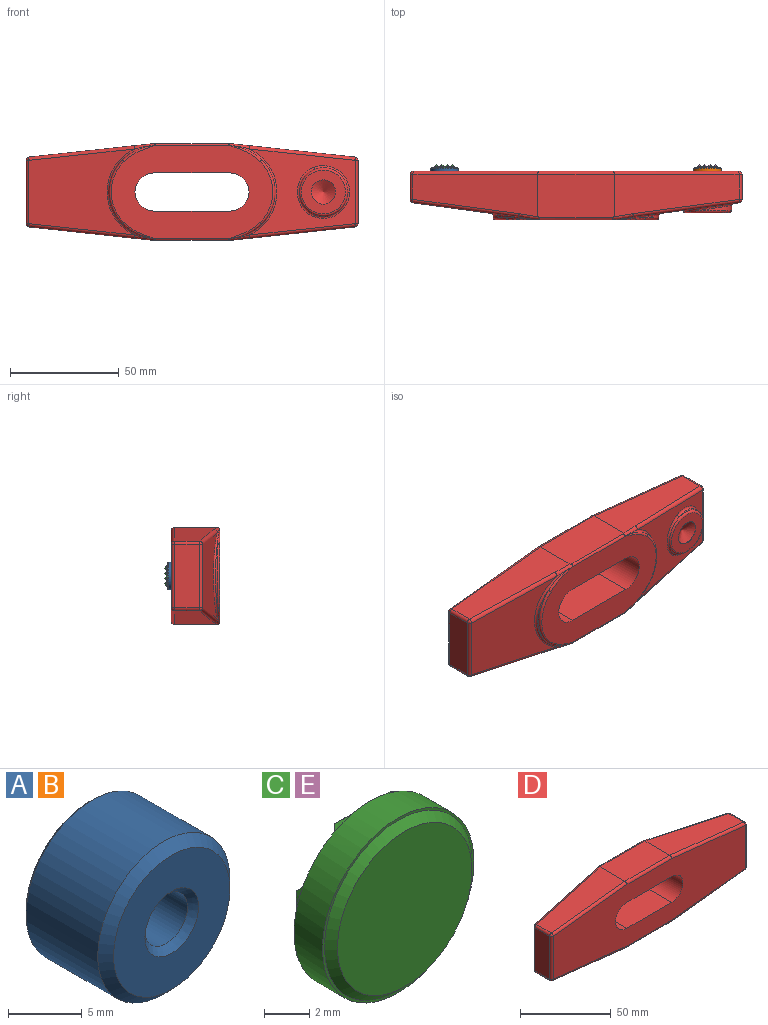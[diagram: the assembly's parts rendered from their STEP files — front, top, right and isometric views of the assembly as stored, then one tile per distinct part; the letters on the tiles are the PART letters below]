
ASSEMBLY  parts=5 mates=4
PART A: 14 faces, bbox 12.7x7.9x12.7 mm
  f0: cone r=2.04mm half-angle=45deg, axis (0,1,0), area 8.7mm2, adj f1,f10
  f1: cylinder r=2.04mm len=5.39mm, axis (0,1,0), area 69.2mm2, adj f0,f2
  f2: cone r=2.58mm half-angle=45deg, axis (0,-1,0), area 11mm2, adj f1,f8
  f3: cylinder r=4.9mm len=9.8mm, axis (0,1,0), area 39.9mm2, adj f4,f10
  f4: cone r=5.16mm half-angle=45deg, axis (0,1,0), area 11.4mm2, adj f3,f9
  f5: cone r=6.35mm half-angle=45deg, axis (0,-1,0), area 14mm2, adj f6,f9
  f6: cylinder r=6.35mm len=12.7mm, axis (0,1,0), area 245.8mm2, adj f5,f7,f11,f12,f13
  f7: cone r=5.59mm half-angle=45deg, axis (0,1,0), area 40.4mm2, adj f6,f8
  f8: plane 11.18x11.18mm, normal (0,-1,0), area 77.2mm2, adj f2,f7
  f9: plane 12.19x12.19mm, normal (0,1,0), area 33.2mm2, adj f4,f5
  f10: plane 9.8x9.8mm, normal (0,1,0), area 56.2mm2, adj f0,f3
  f11: plane 6.89x1.02mm, normal (0,1,0), area 4.7mm2, adj f6,f12
  f12: plane 6.89x3.96mm, normal (1,0,0), area 27.3mm2, adj f6,f11,f13
  f13: plane 6.89x1.02mm, normal (0,-1,0), area 4.7mm2, adj f6,f12
PART B: same geometry as A
PART C: 61 faces, bbox 9.5x3.2x9.5 mm
  f0: cone r=4.2mm half-angle=45deg, axis (0,1,0), area 15.9mm2, adj f38,f39
  f1: cylinder r=4.74mm len=9.47mm, axis (0,-1,0), area 52.9mm2, adj f39,f40
  f2: plane 1.46x0.9mm, normal (0,0.71,0.71), area 0.8mm2, adj f24,f25,f53
  f3: plane 1.46x0.9mm, normal (0,0.71,0.71), area 0.8mm2, adj f22,f23,f54
  f4: plane 1.46x0.9mm, normal (0,0.71,-0.71), area 0.8mm2, adj f18,f21,f55
  f5: plane 1.46x0.9mm, normal (0,0.71,-0.71), area 0.8mm2, adj f19,f20,f56
  f6: plane 1.55x1mm, normal (0,0.71,-0.71), area 1.2mm2, adj f17,f40,f49,f57
  f7: plane 1.55x1mm, normal (0,0.71,-0.71), area 1.2mm2, adj f16,f40,f47,f58
  f8: plane 1.9x0.99mm, normal (0,0.71,0.71), area 1.4mm2, adj f17,f40,f49,f57
  f9: plane 1.9x0.99mm, normal (0,0.71,0.71), area 1.4mm2, adj f16,f40,f47,f58
  f10: plane 1.9x0.99mm, normal (0,0.71,-0.71), area 1.4mm2, adj f15,f40,f43,f59
  f11: plane 1.9x0.99mm, normal (0,0.71,-0.71), area 1.4mm2, adj f14,f40,f41,f60
  f12: plane 1.55x1mm, normal (0,0.71,0.71), area 1.2mm2, adj f15,f40,f43,f59
  f13: plane 1.55x1mm, normal (0,0.71,0.71), area 1.2mm2, adj f14,f40,f41,f60
  f14: plane 1.46x0.9mm, normal (-0.71,0.71,0), area 0.8mm2, adj f11,f13,f60
  f15: plane 1.46x0.9mm, normal (0.71,0.71,0), area 0.8mm2, adj f10,f12,f59
  f16: plane 1.46x0.9mm, normal (-0.71,0.71,0), area 0.8mm2, adj f7,f9,f58
  f17: plane 1.46x0.9mm, normal (0.71,0.71,0), area 0.8mm2, adj f6,f8,f57
  f18: plane 1.55x1mm, normal (-0.71,0.71,0), area 1.2mm2, adj f4,f28,f40,f55
  f19: plane 1.55x1mm, normal (0.71,0.71,0), area 1.2mm2, adj f5,f29,f40,f56
  f20: plane 1.9x0.99mm, normal (-0.71,0.71,0), area 1.4mm2, adj f5,f29,f40,f56
  f21: plane 1.9x0.99mm, normal (0.71,0.71,0), area 1.4mm2, adj f4,f28,f40,f55
  f22: plane 1.55x1mm, normal (0.71,0.71,0), area 1.2mm2, adj f3,f27,f40,f54
  f23: plane 1.9x0.99mm, normal (-0.71,0.71,0), area 1.4mm2, adj f3,f27,f40,f54
  f24: plane 1.9x0.99mm, normal (0.71,0.71,0), area 1.4mm2, adj f2,f26,f40,f53
  f25: plane 1.55x1mm, normal (-0.71,0.71,0), area 1.2mm2, adj f2,f26,f40,f53
  f26: plane 1.98x0.99mm, normal (0,0.71,-0.71), area 1.4mm2, adj f24,f25,f40
  f27: plane 1.98x0.99mm, normal (0,0.71,-0.71), area 1.4mm2, adj f22,f23,f40
  f28: plane 1.98x0.99mm, normal (0,0.71,0.71), area 1.4mm2, adj f18,f21,f40
  f29: plane 1.98x0.99mm, normal (0,0.71,0.71), area 1.4mm2, adj f19,f20,f40
  f30: plane 1.98x0.99mm, normal (0,0.71,-0.71), area 1.4mm2, adj f40,f48,f52
  f31: plane 1.98x0.99mm, normal (0,0.71,-0.71), area 1.4mm2, adj f40,f50,f51
  f32: plane 1.98x0.99mm, normal (0,0.71,0.71), area 1.4mm2, adj f40,f48,f52
  f33: plane 1.98x0.99mm, normal (0,0.71,0.71), area 1.4mm2, adj f40,f50,f51
  f34: plane 1.98x0.99mm, normal (0,0.71,-0.71), area 1.4mm2, adj f40,f42,f46
  f35: plane 1.98x0.99mm, normal (0,0.71,-0.71), area 1.4mm2, adj f40,f44,f45
  f36: plane 1.98x0.99mm, normal (0,0.71,0.71), area 1.4mm2, adj f40,f42,f46
  f37: plane 1.98x0.99mm, normal (0,0.71,0.71), area 1.4mm2, adj f40,f44,f45
  f38: plane 8.41x8.41mm, normal (0,-1,0), area 55.5mm2, adj f0
  f39: plane 9.47x9.47mm, normal (0,-1,0), area 3.7mm2, adj f0,f1
  f40: plane 9.47x9.47mm, normal (0,1,0), area 27.8mm2, adj f1,f6,f7,f8,f9,f10,f11,f12
  f41: plane 1.98x0.99mm, normal (0.71,0.71,0), area 1.4mm2, adj f11,f13,f40
  f42: plane 1.98x0.99mm, normal (-0.71,0.71,0), area 1.4mm2, adj f34,f36,f40
  f43: plane 1.98x0.99mm, normal (-0.71,0.71,0), area 1.4mm2, adj f10,f12,f40
  f44: plane 1.98x0.99mm, normal (0.71,0.71,0), area 1.4mm2, adj f35,f37,f40
  f45: plane 1.98x0.99mm, normal (-0.71,0.71,0), area 1.4mm2, adj f35,f37,f40
  f46: plane 1.98x0.99mm, normal (0.71,0.71,0), area 1.4mm2, adj f34,f36,f40
  f47: plane 1.98x0.99mm, normal (0.71,0.71,0), area 1.4mm2, adj f7,f9,f40
  f48: plane 1.98x0.99mm, normal (-0.71,0.71,0), area 1.4mm2, adj f30,f32,f40
  f49: plane 1.98x0.99mm, normal (-0.71,0.71,0), area 1.4mm2, adj f6,f8,f40
  f50: plane 1.98x0.99mm, normal (0.71,0.71,0), area 1.4mm2, adj f31,f33,f40
  f51: plane 1.98x0.99mm, normal (-0.71,0.71,0), area 1.4mm2, adj f31,f33,f40
  f52: plane 1.98x0.99mm, normal (0.71,0.71,0), area 1.4mm2, adj f30,f32,f40
  f53: cylinder r=4.53mm len=1.98mm, axis (0,1,0), area 0.4mm2, adj f2,f24,f25,f40
  f54: cylinder r=4.53mm len=1.98mm, axis (0,1,0), area 0.4mm2, adj f3,f22,f23,f40
  f55: cylinder r=4.53mm len=1.98mm, axis (0,1,0), area 0.4mm2, adj f4,f18,f21,f40
  f56: cylinder r=4.53mm len=1.98mm, axis (0,1,0), area 0.4mm2, adj f5,f19,f20,f40
  f57: cylinder r=4.53mm len=1.98mm, axis (0,1,0), area 0.4mm2, adj f6,f8,f17,f40
  f58: cylinder r=4.53mm len=1.98mm, axis (0,1,0), area 0.4mm2, adj f7,f9,f16,f40
  f59: cylinder r=4.53mm len=1.98mm, axis (0,1,0), area 0.4mm2, adj f10,f12,f15,f40
  f60: cylinder r=4.53mm len=1.98mm, axis (0,1,0), area 0.4mm2, adj f11,f13,f14,f40
PART D: 67 faces, bbox 154.7x25.3x46.9 mm
  f0: cylinder r=5.56mm len=11.11mm, axis (0,-1,0), area 4.4mm2, adj f1,f2
  f1: cone r=5.56mm half-angle=59deg, axis (0,1,0), area 113.1mm2, adj f0
  f2: plane 20.19x20.19mm, normal (0,1,0), area 223.3mm2, adj f0,f3
  f3: torus R=10.1mm, axis (0,-1,0), area 98.4mm2, adj f2,f4,f66
  f4: bspline ~22.71x8.08mm, area 37.6mm2, adj f3,f5,f6,f7
  f5: bspline ~16.39x12.16mm, area 34.1mm2, adj f4,f6,f7,f66
  f6: bspline ~16.39x12.16mm, area 34.1mm2, adj f4,f5,f7,f66
  f7: plane 51.01x41.83mm, normal (0.13,0.99,0), area 855.1mm2, adj f4,f5,f6,f8,f63,f64,f65
  f8: cylinder r=1.52mm len=48.83mm, axis (0.99,-0.13,0.11), area 117.3mm2, adj f7,f9,f61,f62
  f9: plane 57.38x19.37mm, normal (0.11,0,-0.99), area 884.7mm2, adj f8,f10,f59,f60,f62
  f10: plane 35.05x19.81mm, normal (0,0,-1), area 687.4mm2, adj f9,f11,f56,f57,f58,f62
  f11: plane 57.38x19.37mm, normal (-0.11,0,-0.99), area 884.7mm2, adj f10,f12,f54,f55,f58
  f12: cylinder r=1.52mm len=48.83mm, axis (0.99,0.13,-0.11), area 117.3mm2, adj f11,f13,f53,f58
  f13: plane 51.01x41.83mm, normal (-0.13,0.99,0), area 1317.2mm2, adj f12,f14,f51,f52
  f14: bspline ~43.2x20.11mm, area 75.9mm2, adj f13,f15,f48,f49,f50,f58
  f15: bspline ~9.6x2.84mm, area 17.4mm2, adj f14,f16,f46,f47,f48,f51
  f16: plane 57.38x19.37mm, normal (-0.11,0,0.99), area 884.7mm2, adj f15,f17,f44,f47,f51
  f17: cylinder r=1.52mm len=57.54mm, axis (-0.99,0,-0.11), area 138.1mm2, adj f16,f18,f42,f43
  f18: plane 149.35x41.4mm, normal (0,-1,0), area 4624.3mm2, adj f17,f19,f32,f33,f34,f35,f36,f39
  f19: cylinder r=8.73mm len=22.23mm, axis (0,-1,0), area 609.6mm2, adj f18,f20,f32,f34
  f20: plane 74.22x42.47mm, normal (0,1,0), area 1866.1mm2, adj f19,f21,f23,f30,f31,f32,f33,f34
  f21: torus R=19.62mm, axis (0,-1,0), area 51.7mm2, adj f20,f22,f23,f31
  f22: cylinder r=20.64mm len=29.57mm, axis (0,-1,0), area 0mm2, adj f21,f65
  f23: bspline ~14.22x7.41mm, area 16.5mm2, adj f20,f21,f24,f46,f65
  f24: bspline ~9.6x2.84mm, area 17.4mm2, adj f23,f25,f46,f47,f64,f65
  f25: plane 57.38x19.37mm, normal (0.11,0,0.99), area 884.7mm2, adj f24,f26,f35,f47,f64
  f26: cylinder r=1.52mm len=11.43mm, axis (0,-1,0), area 25.5mm2, adj f25,f27,f28,f29
  f27: plane 29.01x11.43mm, normal (1,0,0), area 331.7mm2, adj f26,f36,f60,f63
  f28: sphere r=1.52mm, area 4.7mm2, adj f26,f35,f36
  f29: sphere r=1.52mm, area 3.2mm2, adj f26,f63,f64
  f30: torus R=19.62mm, axis (0,-1,0), area 51.7mm2, adj f20,f48,f49,f50
  f31: bspline ~14.22x7.41mm, area 16.5mm2, adj f20,f21,f57,f62,f65
  f32: plane 34.93x22.23mm, normal (0,0,1), area 776.2mm2, adj f18,f19,f20,f33
  f33: cylinder r=8.73mm len=22.23mm, axis (0,-1,0), area 609.6mm2, adj f18,f20,f32,f34
  f34: plane 34.93x22.23mm, normal (0,0,-1), area 776.2mm2, adj f18,f19,f20,f33
  f35: cylinder r=1.52mm len=57.54mm, axis (-0.99,0,0.11), area 138.1mm2, adj f18,f25,f28,f43
  f36: cylinder r=1.52mm len=29.01mm, axis (0,0,1), area 69.5mm2, adj f18,f27,f28,f37,f38
  f37: sphere r=1.52mm, area 0.4mm2, adj f36,f59
  f38: sphere r=1.52mm, area 1.2mm2, adj f36,f59,f60
  f39: cylinder r=1.52mm len=29.01mm, axis (0,0,1), area 69.5mm2, adj f18,f40,f41,f42
  f40: plane 29.01x11.43mm, normal (-1,0,0), area 331.7mm2, adj f39,f44,f52,f54
  f41: sphere r=1.52mm, area 4.7mm2, adj f39,f54,f55
  f42: sphere r=1.52mm, area 3.4mm2, adj f17,f39,f44
  f43: cylinder r=1.52mm len=34.93mm, axis (1,0,0), area 83.4mm2, adj f17,f18,f35,f47
  f44: cylinder r=1.52mm len=11.43mm, axis (0,-1,0), area 25.5mm2, adj f16,f40,f42,f45
  f45: sphere r=1.52mm, area 2mm2, adj f44,f51,f52
  f46: cylinder r=1.02mm len=35.59mm, axis (-1,0,0), area 54.6mm2, adj f15,f20,f23,f24,f47,f48
  f47: plane 35.05x19.81mm, normal (0,0,1), area 687.4mm2, adj f15,f16,f24,f25,f43,f46
  f48: bspline ~14.22x7.41mm, area 16.5mm2, adj f14,f15,f20,f30,f46
  f49: cylinder r=20.64mm len=29.57mm, axis (0,-1,0), area 0mm2, adj f14,f30
  f50: bspline ~14.22x7.41mm, area 16.5mm2, adj f14,f20,f30,f57,f58
  f51: cylinder r=1.52mm len=48.83mm, axis (-0.99,-0.13,-0.11), area 117.3mm2, adj f13,f15,f16,f45
  f52: cylinder r=1.52mm len=29.01mm, axis (0,0,1), area 63.5mm2, adj f13,f40,f45,f53
  f53: sphere r=1.52mm, area 2mm2, adj f12,f52,f54
  f54: cylinder r=1.52mm len=11.43mm, axis (0,-1,0), area 25.5mm2, adj f11,f40,f41,f53
  f55: cylinder r=1.52mm len=57.54mm, axis (0.99,0,-0.11), area 138.1mm2, adj f11,f18,f41,f56
  f56: cylinder r=1.52mm len=34.93mm, axis (-1,0,0), area 83.4mm2, adj f10,f18,f55,f59
  f57: cylinder r=1.02mm len=35.59mm, axis (1,0,0), area 54.6mm2, adj f10,f20,f31,f50,f58,f62
  f58: bspline ~9.6x2.84mm, area 17.4mm2, adj f10,f11,f12,f14,f50,f57
  f59: cylinder r=1.52mm len=57.54mm, axis (0.99,0,0.11), area 138.1mm2, adj f9,f18,f37,f38,f56
  f60: cylinder r=1.52mm len=11.43mm, axis (0,-1,0), area 25.5mm2, adj f9,f27,f38,f61
  f61: sphere r=1.52mm, area 2mm2, adj f8,f60,f63
  f62: bspline ~9.6x2.84mm, area 17.4mm2, adj f8,f9,f10,f31,f57,f65
  f63: cylinder r=1.52mm len=29.01mm, axis (0,0,1), area 63.5mm2, adj f7,f27,f29,f61
  f64: cylinder r=1.52mm len=48.83mm, axis (-0.99,0.13,0.11), area 117.3mm2, adj f7,f24,f25,f29
  f65: bspline ~43.2x20.11mm, area 75.9mm2, adj f7,f22,f23,f24,f31,f62
  f66: cylinder r=11.11mm len=22.23mm, axis (0,1,0), area 51mm2, adj f3,f5,f6
PART E: same geometry as C
PLACE A t=(-98.79,-12.12,-32.54)mm
PLACE B t=(21.86,-12.12,-32.54)mm
PLACE C t=(-98.79,-12.12,-32.54)mm
PLACE D rot(axis=(1,0,0),180deg) t=(-38.46,-5.77,-32.54)mm
PLACE E t=(21.86,-12.12,-32.54)mm
MATE fastened D.f0 <-> B.f0  axis (0,-1,0) through (21.86,-24.82,-32.54)mm
MATE fastened B.f0 <-> E.f0  axis (0,1,0) through (21.86,-5.77,-32.54)mm
MATE fastened D.f2 <-> A.f0  axis (0,-1,0) through (-98.79,-24.82,-32.54)mm
MATE fastened A.f0 <-> C.f0  axis (0,1,0) through (-98.79,-5.77,-32.54)mm
